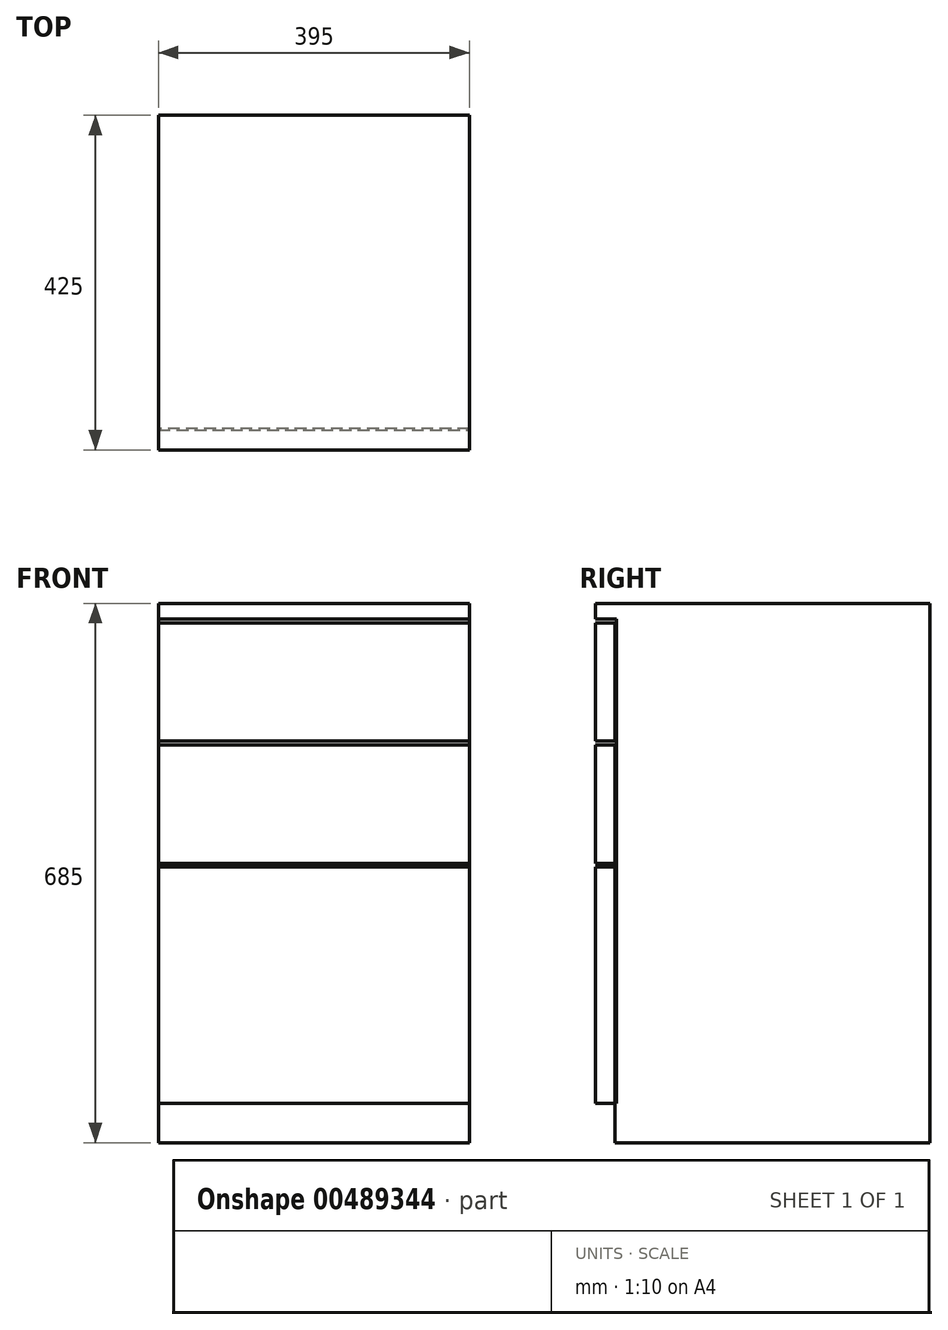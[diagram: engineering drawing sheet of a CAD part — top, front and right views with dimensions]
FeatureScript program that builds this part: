
annotation { "Feature Type Name" : "Feature", "Feature Type Description" : "" }
export const myFeature = defineFeature(function(context is Context, id is Id, definition is map)
    precondition{}
    {
        {
            var Q0;
            Q0=qCreatedBy(makeId("Top.planeOp"),FACE);
            var sketch = newSketch(context, id + "F0", { "sketchPlane" : qUnion([Q0])});
            skLineSegment(sketch, "E0.bottom", {"start": v(197.5, -212.5) * mm, "end": v(-197.5, -212.5) * mm});
            skLineSegment(sketch, "E0.top", {"start": v(197.5, 212.5) * mm, "end": v(-197.5, 212.5) * mm});
            skLineSegment(sketch, "E0.left", {"start": v(197.5, -212.5) * mm, "end": v(197.5, 212.5) * mm});
            skLineSegment(sketch, "E0.right", {"start": v(-197.5, -212.5) * mm, "end": v(-197.5, 212.5) * mm});
            skPoint(sketch, "E0.middle", {"position": v(0, 0) * mm});
            skSolve(sketch);
        }
        {
            var Q0;
            Q0=makeQuery(id+"F0.imprint","IMPRINT",FACE,{"disambiguationData":[TD([[makeQuery(id+"F0.imprint","IMPRINT",EDGE,{"derivedFrom":sQuery(id+"F0.wireOp",EDGE,"E0.bottom")}),-1.0]])]});
            extrude(context, id + "F1", {"entities" : qUnion([Q0]), "depth" : 685 * mm});
        }
        {
            var Q0;
            Q0=makeQuery(id+"F1.opExtrude","SWEPT_FACE",FACE,{"disambiguationData":[OSD([sQuery(id+"F0.wireOp",EDGE,"E0.bottom")])]});
            var sketch = newSketch(context, id + "F2", { "sketchPlane" : qUnion([Q0])});
            skLineSegment(sketch, "E1.bottom", {"start": v(-197.5, 355) * mm, "end": v(197.5, 355) * mm});
            skLineSegment(sketch, "E1.top", {"start": v(-197.5, 350) * mm, "end": v(197.5, 350) * mm});
            skLineSegment(sketch, "E1.left", {"start": v(-197.5, 355) * mm, "end": v(-197.5, 350) * mm});
            skLineSegment(sketch, "E1.right", {"start": v(197.5, 355) * mm, "end": v(197.5, 350) * mm});
            skLineSegment(sketch, "E2.bottom", {"start": v(-197.5, 665) * mm, "end": v(197.5, 665) * mm});
            skLineSegment(sketch, "E2.top", {"start": v(-197.5, 660) * mm, "end": v(197.5, 660) * mm});
            skLineSegment(sketch, "E2.left", {"start": v(-197.5, 665) * mm, "end": v(-197.5, 660) * mm});
            skLineSegment(sketch, "E2.right", {"start": v(197.5, 665) * mm, "end": v(197.5, 660) * mm});
            skLineSegment(sketch, "E3.bottom", {"start": v(-197.5, 510) * mm, "end": v(197.5, 510) * mm});
            skLineSegment(sketch, "E3.top", {"start": v(-197.5, 505) * mm, "end": v(197.5, 505) * mm});
            skLineSegment(sketch, "E3.left", {"start": v(-197.5, 510) * mm, "end": v(-197.5, 505) * mm});
            skLineSegment(sketch, "E3.right", {"start": v(197.5, 510) * mm, "end": v(197.5, 505) * mm});
            skLineSegment(sketch, "E4.bottom", {"start": v(-197.5, 0) * mm, "end": v(197.5, 0) * mm});
            skLineSegment(sketch, "E4.top", {"start": v(-197.5, 50) * mm, "end": v(197.5, 50) * mm});
            skLineSegment(sketch, "E4.left", {"start": v(-197.5, 0) * mm, "end": v(-197.5, 50) * mm});
            skLineSegment(sketch, "E4.right", {"start": v(197.5, 0) * mm, "end": v(197.5, 50) * mm});
            skSolve(sketch);
        }
        {
            var Q0;
            Q0 = qSketchRegion(id + "F2", true);
            extrude(context, id + "F3", {"entities" : qUnion([Q0]), "operationType" : NewBodyOperationType.REMOVE, "oppositeDirection" : true, "depth" : 25 * mm});
        }
        {
            var Q0;
            Q0=makeQuery(id+"F1.opExtrude","SWEPT_FACE",FACE,{"disambiguationData":[OSD([sQuery(id+"F0.wireOp",EDGE,"E0.right")])]});
            var sketch = newSketch(context, id + "F4", { "sketchPlane" : qUnion([Q0])});
            skLineSegment(sketch, "E5.bottom", {"start": v(187.5, 665) * mm, "end": v(185.5, 665) * mm});
            skLineSegment(sketch, "E5.top", {"start": v(187.5, 50) * mm, "end": v(185.5, 50) * mm});
            skLineSegment(sketch, "E5.left", {"start": v(187.5, 665) * mm, "end": v(187.5, 50) * mm});
            skLineSegment(sketch, "E5.right", {"start": v(185.5, 665) * mm, "end": v(185.5, 50) * mm});
            skSolve(sketch);
        }
        {
            var Q0;
            Q0 = qSketchRegion(id + "F4", true);
            extrude(context, id + "F5", {"entities" : qUnion([Q0]), "operationType" : NewBodyOperationType.REMOVE, "endBound" : BoundingType.THROUGH_ALL, "oppositeDirection" : true, "depth" : 25 * mm});
        }
    });
